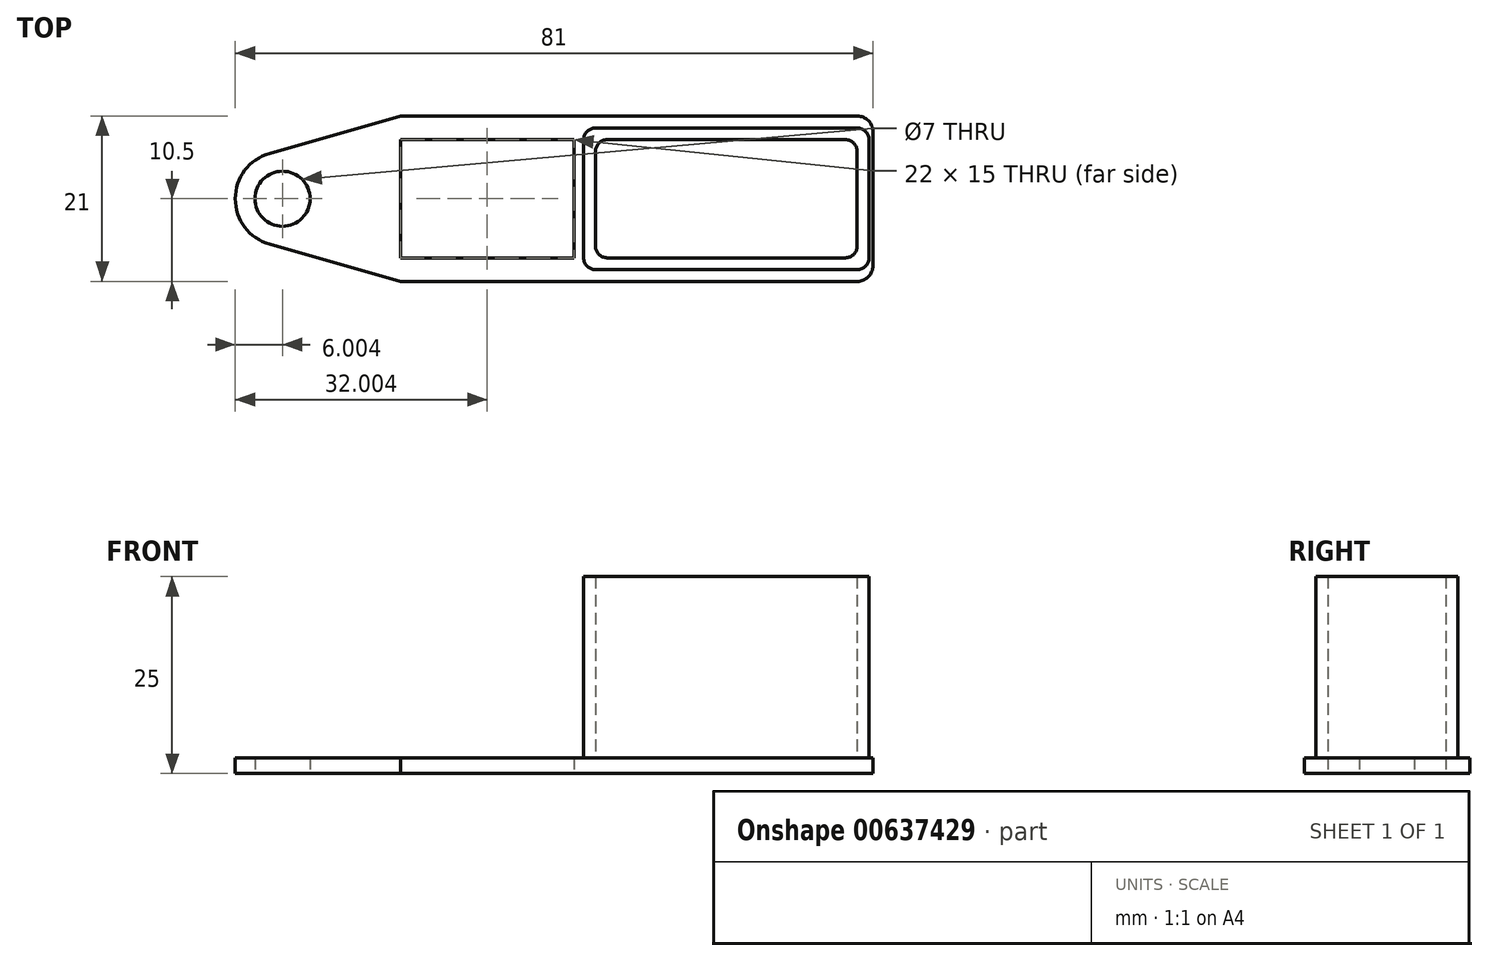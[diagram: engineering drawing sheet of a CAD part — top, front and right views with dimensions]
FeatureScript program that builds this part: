
annotation { "Feature Type Name" : "Feature", "Feature Type Description" : "" }
export const myFeature = defineFeature(function(context is Context, id is Id, definition is map)
    precondition{}
    {
        {
            var Q0;
            Q0=qCreatedBy(makeId("Top.planeOp"),FACE);
            var sketch = newSketch(context, id + "F0", { "sketchPlane" : qUnion([Q0])});
            skLineSegment(sketch, "E0", {"start": v(-21.87, 0) * mm, "end": v(55.7, 0) * mm, "construction": true});
            skArc(sketch, "E1", {"start": v(-23.5, 5.77) * mm, "mid": v(-27.87, 0) * mm, "end": v(-23.5, -5.77) * mm, "construction": true});
            skCircle(sketch, "E2", {"center": v(-21.87, 0) * mm, "radius": 3.5 * mm});
            skLineSegment(sketch, "E3", {"start": v(-6.87, -10.5) * mm, "end": v(-6.87, 10.5) * mm, "construction": true});
            skLineSegment(sketch, "E4", {"start": v(-6.87, 10.5) * mm, "end": v(53.32, 10.5) * mm, "construction": true});
            skLineSegment(sketch, "E5.0", {"start": v(-6.87, -10.5) * mm, "end": v(51.13, -10.5) * mm});
            skLineSegment(sketch, "E6", {"start": v(-6.87, -10.5) * mm, "end": v(-23.5, -5.77) * mm});
            skLineSegment(sketch, "E7", {"start": v(53.13, -8.5) * mm, "end": v(53.13, 8.5) * mm});
            skLineSegment(sketch, "E8", {"start": v(51.13, 10.5) * mm, "end": v(-6.87, 10.5) * mm});
            skLineSegment(sketch, "E9.MirrorCS", {"start": v(-6.87, 10.5) * mm, "end": v(-23.5, 5.77) * mm});
            skPoint(sketch, "E10.visualSharp", {"position": v(53.13, 10.5) * mm});
            skArc(sketch, "E10.filletArc", {"start": v(53.13, 8.5) * mm, "mid": v(52.55, 9.91) * mm, "end": v(51.13, 10.5) * mm});
            skPoint(sketch, "E11.visualSharp", {"position": v(53.13, -10.5) * mm});
            skArc(sketch, "E11.filletArc", {"start": v(51.13, -10.5) * mm, "mid": v(52.55, -9.91) * mm, "end": v(53.13, -8.5) * mm});
            skArc(sketch, "E12", {"start": v(-23.5, 5.77) * mm, "mid": v(-27.87, 0) * mm, "end": v(-23.5, -5.77) * mm});
            skLineSegment(sketch, "E13", {"start": v(15.13, 10.5) * mm, "end": v(15.13, 7.5) * mm, "construction": true});
            skLineSegment(sketch, "E14", {"start": v(-6.87, 7.5) * mm, "end": v(15.13, 7.5) * mm, "construction": true});
            skLineSegment(sketch, "E15.MirrorCS", {"start": v(-6.87, -7.5) * mm, "end": v(15.13, -7.5) * mm, "construction": true});
            skPoint(sketch, "E16.oppositeSnap0", {"position": v(24.96, 7.5) * mm});
            skLineSegment(sketch, "E16.bottom", {"start": v(-6.87, 7.5) * mm, "end": v(15.13, 7.5) * mm});
            skLineSegment(sketch, "E16.top", {"start": v(-6.87, 7.5) * mm, "end": v(15.13, 7.5) * mm});
            skLineSegment(sketch, "E16.left", {"start": v(-6.87, 7.5) * mm, "end": v(-6.87, 7.5) * mm});
            skLineSegment(sketch, "E16.right", {"start": v(15.13, 7.5) * mm, "end": v(15.13, 7.5) * mm});
            skLineSegment(sketch, "E17.bottom", {"start": v(15.13, -7.5) * mm, "end": v(-6.87, -7.5) * mm});
            skLineSegment(sketch, "E17.top", {"start": v(15.13, -7.5) * mm, "end": v(-6.87, -7.5) * mm});
            skLineSegment(sketch, "E17.left", {"start": v(15.13, -7.5) * mm, "end": v(15.13, -7.5) * mm});
            skLineSegment(sketch, "E17.right", {"start": v(-6.87, -7.5) * mm, "end": v(-6.87, -7.5) * mm});
            skLineSegment(sketch, "E18.trimOffspring", {"start": v(15.13, -10.5) * mm, "end": v(15.13, -10.55) * mm, "construction": true});
            skPoint(sketch, "E19.orphan", {"position": v(14.1, -7.5) * mm});
            skPoint(sketch, "E20.orphan", {"position": v(14.1, 7.5) * mm});
            skPoint(sketch, "E21.start.orphan", {"position": v(15.13, 11.03) * mm});
            skLineSegment(sketch, "E22", {"start": v(-6.87, 7.5) * mm, "end": v(-6.87, -7.5) * mm});
            skLineSegment(sketch, "E23", {"start": v(15.13, 7.5) * mm, "end": v(15.13, -7.5) * mm});
            skPoint(sketch, "E24.orphan", {"position": v(15.13, 25.55) * mm});
            skPoint(sketch, "E25.orphan", {"position": v(35.82, 7.5) * mm});
            skPoint(sketch, "E26.orphan", {"position": v(35.82, -7.5) * mm});
            skLineSegment(sketch, "E27", {"start": v(19.38, 7.5) * mm, "end": v(49.63, 7.5) * mm, "construction": true});
            skLineSegment(sketch, "E28.MirrorCS", {"start": v(19.38, -7.5) * mm, "end": v(49.63, -7.5) * mm, "construction": true});
            skLineSegment(sketch, "E29", {"start": v(17.88, 7.5) * mm, "end": v(17.88, -7.5) * mm, "construction": true});
            skLineSegment(sketch, "E30", {"start": v(51.13, 7.5) * mm, "end": v(51.13, -7.5) * mm, "construction": true});
            skLineSegment(sketch, "E31.bottom", {"start": v(17.88, -7.5) * mm, "end": v(51.13, -7.5) * mm});
            skLineSegment(sketch, "E31.top", {"start": v(17.88, 7.5) * mm, "end": v(51.13, 7.5) * mm});
            skLineSegment(sketch, "E31.left", {"start": v(17.88, -6) * mm, "end": v(17.88, 6) * mm});
            skLineSegment(sketch, "E31.right", {"start": v(51.13, -6) * mm, "end": v(51.13, 6) * mm});
            skLineSegment(sketch, "E32.0", {"start": v(16.38, -7.5) * mm, "end": v(16.38, 7.5) * mm});
            skLineSegment(sketch, "E33.0", {"start": v(17.88, 9) * mm, "end": v(51.13, 9) * mm});
            skLineSegment(sketch, "E34.0", {"start": v(17.88, -9) * mm, "end": v(51.13, -9) * mm});
            skLineSegment(sketch, "E35.0", {"start": v(52.63, -7.5) * mm, "end": v(52.63, 7.5) * mm});
            skLineSegment(sketch, "E36", {"start": v(17.88, 9) * mm, "end": v(17.88, 9) * mm});
            skLineSegment(sketch, "E37", {"start": v(16.38, 7.5) * mm, "end": v(16.38, 7.5) * mm});
            skPoint(sketch, "E38.orphan", {"position": v(14.1, 9) * mm});
            skPoint(sketch, "E39.trimOffspring.end.orphan", {"position": v(53.13, 7.5) * mm});
            skPoint(sketch, "E40.trimOffspring.end.orphan", {"position": v(53.13, -7.5) * mm});
            skLineSegment(sketch, "E41", {"start": v(17.88, -9) * mm, "end": v(17.88, -9) * mm});
            skLineSegment(sketch, "E42", {"start": v(16.38, -7.5) * mm, "end": v(16.38, -7.5) * mm});
            skLineSegment(sketch, "E43", {"start": v(52.63, 7.5) * mm, "end": v(52.63, 7.5) * mm});
            skLineSegment(sketch, "E44", {"start": v(52.63, -7.5) * mm, "end": v(52.63, -7.5) * mm});
            skLineSegment(sketch, "E45.trimOffspring", {"start": v(53.07, 9) * mm, "end": v(58.13, 9) * mm});
            skLineSegment(sketch, "E46.trimOffspring", {"start": v(53.07, -9) * mm, "end": v(58.13, -9) * mm});
            skPoint(sketch, "E47.visualSharp", {"position": v(52.63, 9) * mm});
            skArc(sketch, "E47.filletArc", {"start": v(52.63, 7.5) * mm, "mid": v(52.2, 8.56) * mm, "end": v(51.13, 9) * mm});
            skPoint(sketch, "E48.visualSharp", {"position": v(52.63, -9) * mm});
            skArc(sketch, "E48.filletArc", {"start": v(51.13, -9) * mm, "mid": v(52.2, -8.56) * mm, "end": v(52.63, -7.5) * mm});
            skPoint(sketch, "E49.visualSharp", {"position": v(16.38, 9) * mm});
            skArc(sketch, "E49.filletArc", {"start": v(17.88, 9) * mm, "mid": v(16.82, 8.56) * mm, "end": v(16.38, 7.5) * mm});
            skPoint(sketch, "E50.visualSharp", {"position": v(16.38, -9) * mm});
            skArc(sketch, "E50.filletArc", {"start": v(16.38, -7.5) * mm, "mid": v(16.82, -8.56) * mm, "end": v(17.88, -9) * mm});
            skArc(sketch, "E51.filletArc", {"start": v(19.38, 7.5) * mm, "mid": v(18.32, 7.06) * mm, "end": v(17.88, 6) * mm});
            skArc(sketch, "E52.filletArc", {"start": v(17.88, -6) * mm, "mid": v(18.32, -7.06) * mm, "end": v(19.38, -7.5) * mm});
            skArc(sketch, "E53.filletArc", {"start": v(51.13, 6) * mm, "mid": v(50.7, 7.06) * mm, "end": v(49.63, 7.5) * mm});
            skArc(sketch, "E54.filletArc", {"start": v(49.63, -7.5) * mm, "mid": v(50.7, -7.06) * mm, "end": v(51.13, -6) * mm});
            skSolve(sketch);
        }
        {
            var Q0;
            Q0=makeQuery(id+"F0.imprint","IMPRINT",FACE,{"disambiguationData":[TD([[makeQuery(id+"F0.imprint","IMPRINT",EDGE,{"derivedFrom":sQuery(id+"F0.wireOp",EDGE,"E2")}),-1.0]])]});
            extrude(context, id + "F1", {"entities" : qUnion([Q0]), "depth" : 2 * mm, "offsetDistance" : 25 * mm});
        }
        {
            var Q0;
            Q0=makeQuery(id+"F0.imprint","IMPRINT",FACE,{"disambiguationData":[TD([[makeQuery(id+"F0.imprint","IMPRINT",EDGE,{"derivedFrom":sQuery(id+"F0.wireOp",EDGE,"E31.left")}),1.0]])]});
            extrude(context, id + "F2", {"entities" : qUnion([Q0]), "operationType" : NewBodyOperationType.ADD, "depth" : 25 * mm, "offsetDistance" : 25 * mm});
        }
        {
            var Q0;
            Q0=makeQuery(id+"F0.imprint","IMPRINT",FACE,{"disambiguationData":[TD([[makeQuery(id+"F0.imprint","IMPRINT",EDGE,{"derivedFrom":sQuery(id+"F0.wireOp",EDGE,"E31.left")}),-1.0]])]});
            extrude(context, id + "F3", {"entities" : qUnion([Q0]), "operationType" : NewBodyOperationType.ADD, "depth" : 2 * mm, "offsetDistance" : 25 * mm});
        }
    });
